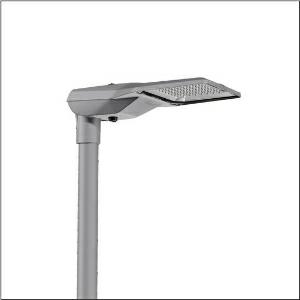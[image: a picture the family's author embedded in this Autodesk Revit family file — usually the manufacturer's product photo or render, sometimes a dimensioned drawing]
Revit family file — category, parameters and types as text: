
# Revit family: streetlight_sl_21_iq_midi___p0_8a_5xe3u31y08nb_1433
name_source: partatom
category: Lighting Fixtures
units: mm (PartAtom-declared; Revit-internal decimal feet)

## family parameters
Cut with Voids When Loaded = No
Host = Face
Light Source = No
Part Type = Normal
Room Calculation Point = No
Round Connector Dimension = Use Diameter
Shared = No

## types (1)
- --- (1 x LED, 21740 lm, 136.6 W, 3000K)
    Apparent Load = 137 VA
    CIE Flux Codes = 36 69 97 100 100
    Color Rendering = 70
    Color Temperature = 3000K
    Default Elevation = 1800 mm
    Description = Streetlight SL 21 iQ midi, mast luminaire, primary light control with lens, of PMMA, primary optical cover: cover, of toughened safety glass, transparent, light distribution: P0.8a, light emission: direct distribution, primary light characteristic: asymmetric, installation type: post-top, side-entry, LED, High Power LED, rated luminous flux: 21.740lm, luminous efficacy: 159lm/W, light colour: 730, colour temperature: 3000K, control gear: iQ-Street Remote, D4i with power reduction, control: pre-setting: logarithmic dimming characteristic, Street-Remote, Auto-Match, Temp-Guard, Lumen-Switch, Night-Set, Smart-Wire, Light-Fading, Desk-Remote (wireless, voltage-free reading and setting of iQ features in the workshop via application-optimized NFC function/RFID function), optimised constant luminous flux control (CLO 2.0), mains connection: 230..240V, AC, 50/60Hz, start of lifetime: 137W, end of service life: 144W, reduction: 61W, luminaire housing, of diecast aluminium, powder-coated, Siteco® metallic grey (DB 702S), corrosivity category C5 mid according to DIN EN ISO 12944, please order mast flange separately, inclination adjustable: 0°, 5°, 10°, 15°, sealing non-destructively replaceable, multi-level sealing system, length: 644mm, width: 335mm, height: 110mm, mast flange for spigot size: 42mm (side-entry): 5XC10008XM4, 60/48mm (side-entry/post-top): 5XC10108XM2, 76/60mm (side-entry/post-top): 5XC10108XM1, mounting height: 4..8m, Smart Interface below and above, protection rating (complete): IP66, insulation class (complete): insulation class II (safety insulation), certification: CE, ENEC, ENEC+, VDE, impact resistance: IK10, permissible operating ambient temperature for outdoor applications: -40..+50°C, standard-compliant lighting for roads and squares, packaging unit: 1 piece

Light Distribution: P0.8a
    Height = 111 mm
    Lamp = 1 x LED
    Lamp Light Flux = 21740 lm
    Lamp Power = 136.6 W
    Lamp count = 1
    Length = 644 mm
    Luminous efficacy = 159 lm/W
    Manufacturer = Siteco
    ModVariant = No
    Model = 5XE3U31Y08NB
    Number of Poles = 1
    OnlyDefault = Yes
    Power Factor = 1
    Product Name = Streetlight SL 21 iQ midi | P0.8a
    Product group = mast luminaire | pylon top
    ProductGroupID = 6100
    Protection Class = Protection class II
    Protection Degree = IP 66
    RLX_Detail_Level = 1
    RLX_Emergency_Light_Flux = 0 lm
    RLX_Emergency_Type = 0
    RLX_Emergency_Type_DB = No
    RlxData = <blob elided: 27125 chars, md5=9d660bc7>
    Socket = socket
    Standby Power = 0 W
    System Light Flux = 21740 lm
    System Power = 137 W
    Type Comments = factory setting: luminous flux: 100 % | dim-lin: 254 | 733 mA
    Type Image = l_1004304.jpg
    URL = http://relux.com
    VarID = @adj_071984
    Voltage = 0 V
    Weight = 0.00 kg
    Width = 336 mm

## geometry (parser evidence)
native form markers: Blend x4, Sweep x9
no freeform markers — native parametric forms only
